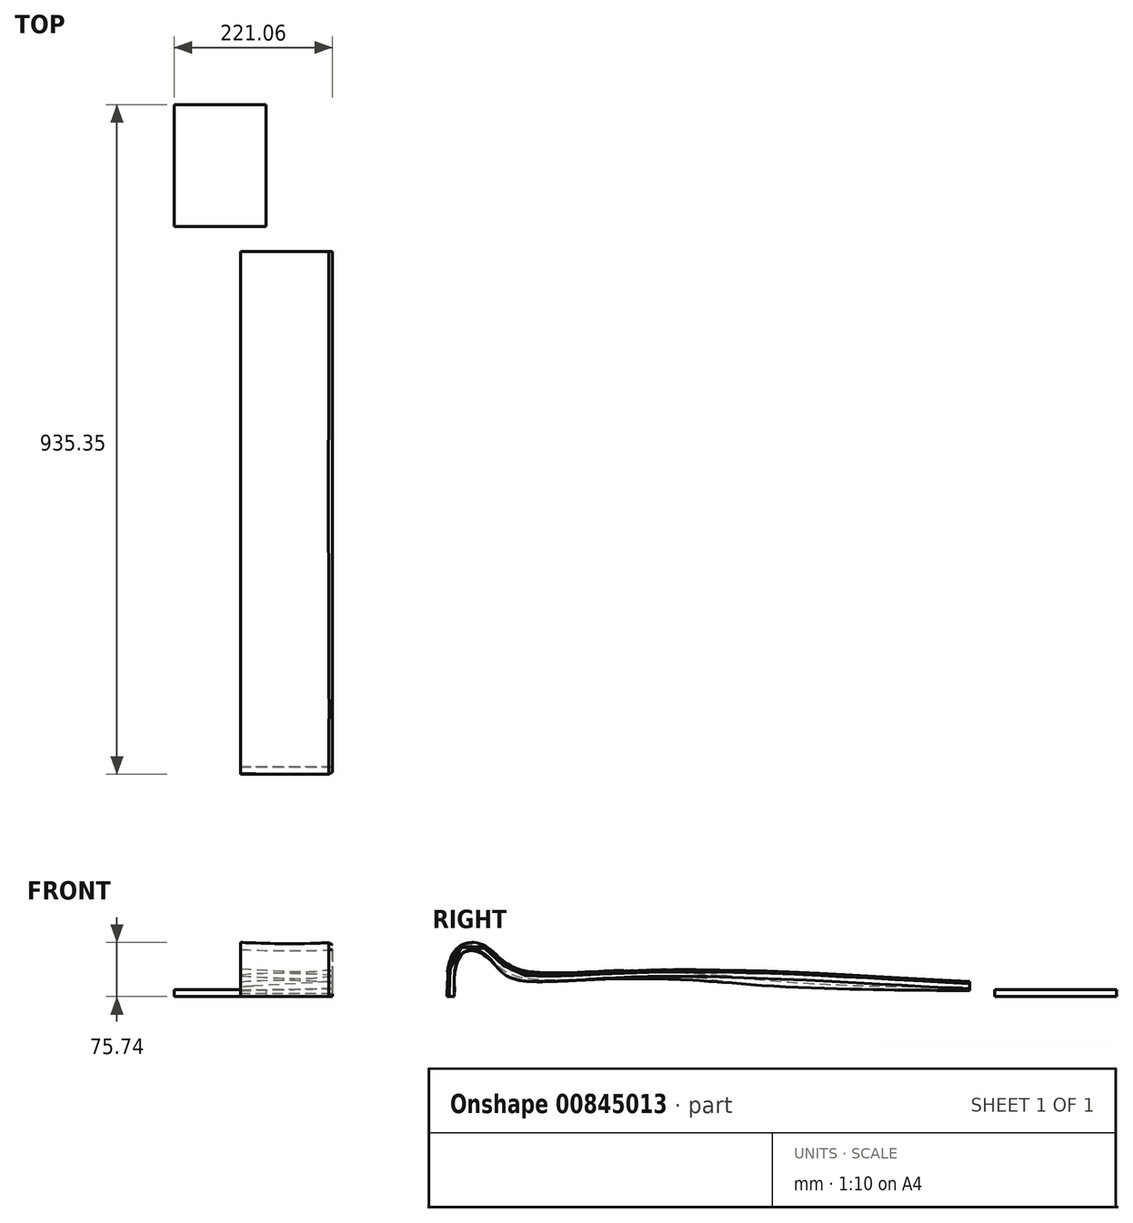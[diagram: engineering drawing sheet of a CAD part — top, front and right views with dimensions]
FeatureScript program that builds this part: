
annotation { "Feature Type Name" : "Feature", "Feature Type Description" : "" }
export const myFeature = defineFeature(function(context is Context, id is Id, definition is map)
    precondition{}
    {
        {
            var Q0;
            Q0=qCreatedBy(makeId("Right.planeOp"),FACE);
            var sketch = newSketch(context, id + "F0", { "sketchPlane" : qUnion([Q0])});
            skLineSegment(sketch, "E0", {"start": v(0, 4.3) * mm, "end": v(0, 0) * mm});
            skLineSegment(sketch, "E1", {"start": v(0, 0) * mm, "end": v(10, 0) * mm});
            skLineSegment(sketch, "E2", {"start": v(10, 0) * mm, "end": v(10, 4.3) * mm});
            skFitSpline(sketch, "E3", {"points": [v(10, 4.3) * mm, v(10, 9.47) * mm, v(10.81, 35.91) * mm, v(20.4, 60) * mm, v(37.7, 65.58) * mm, v(59.21, 54.06) * mm, v(82, 29.92) * mm, v(145.43, 21.16) * mm, v(328.73, 28.44) * mm, v(730, 11.2) * mm], "startDerivative": vector(2.28, 304.75) * mm, "endDerivative": vector(317.82, 1.74) * mm});
            skFitSpline(sketch, "E4", {"points": [v(0, 4.3) * mm, v(0, 9.47) * mm, v(0.81, 35.91) * mm, v(13.55, 67.28) * mm, v(37.7, 75.58) * mm, v(66.24, 61.18) * mm, v(87.9, 37.99) * mm, v(145.43, 31.16) * mm, v(328.73, 38.44) * mm, v(730, 21.2) * mm], "startDerivative": vector(0, 134.34) * mm, "endDerivative": vector(1575.84, -88.39) * mm});
            skLineSegment(sketch, "E5", {"start": v(730, 11.2) * mm, "end": v(730, 21.2) * mm});
            skSolve(sketch);
        }
        {
            var Q0;
            Q0=qCreatedBy(makeId("Right.planeOp"),FACE);
            cPlane(context, id + "F1", {"entities" : qUnion([Q0]), "cplaneType" : CPlaneType.OFFSET, "offset" : 128.5 * mm, "oppositeDirection" : true, "width" : 152.4 * mm, "height" : 152.4 * mm});
        }
        {
            var Q0;
            Q0=qCreatedBy(id+"F1.planeOp",FACE);
            var sketch = newSketch(context, id + "F2", { "sketchPlane" : qUnion([Q0])});
            skLineSegment(sketch, "E6", {"start": v(0, 4.3) * mm, "end": v(0, 0) * mm});
            skLineSegment(sketch, "E7", {"start": v(0, 0) * mm, "end": v(10, 0) * mm});
            skLineSegment(sketch, "E8", {"start": v(10, 0) * mm, "end": v(10, 4.3) * mm});
            skFitSpline(sketch, "E9", {"points": [v(10, 4.3) * mm, v(10.47, 9.4) * mm, v(10.81, 35.91) * mm, v(20.4, 60) * mm, v(37.7, 65.58) * mm, v(59.21, 54.06) * mm, v(82, 29.92) * mm, v(145.43, 21.16) * mm, v(328.73, 28.44) * mm, v(402.6, 19.18) * mm, v(589.23, 10) * mm, v(694, 8.62) * mm, v(730, 8.52) * mm], "startDerivative": vector(51.41, 302.7) * mm, "endDerivative": vector(431.3, 10.14) * mm});
            skFitSpline(sketch, "E10", {"points": [v(0, 4.3) * mm, v(0.47, 9.4) * mm, v(0.81, 35.91) * mm, v(13.55, 67.28) * mm, v(37.7, 75.58) * mm, v(66.24, 61.18) * mm, v(87.9, 37.99) * mm, v(145.43, 31.16) * mm, v(328.73, 38.44) * mm, v(402.6, 27.68) * mm, v(589.23, 15) * mm, v(694, 13.62) * mm, v(730, 13.52) * mm], "startDerivative": vector(0, 134.34) * mm, "endDerivative": vector(521.26, 14.92) * mm});
            skLineSegment(sketch, "E11", {"start": v(730, 8.52) * mm, "end": v(730, 13.52) * mm});
            skSolve(sketch);
        }
        {
            var Q0;
            Q0=makeQuery(id+"F0.imprint","IMPRINT",FACE,{"disambiguationData":[TD([[makeQuery(id+"F0.imprint","IMPRINT",EDGE,{"derivedFrom":sQuery(id+"F0.wireOp",EDGE,"E0")}),1.0]])]});
            var Q1;
            Q1=makeQuery(id+"F2.imprint","IMPRINT",FACE,{"disambiguationData":[TD([[makeQuery(id+"F2.imprint","IMPRINT",EDGE,{"derivedFrom":sQuery(id+"F2.wireOp",EDGE,"E6")}),1.0]])]});
            loft(context, id + "F3", {"sheetProfilesArray" : [{ "sheetProfileEntities" : qUnion([Q0]) }, { "sheetProfileEntities" : qUnion([Q1]) }]});
        }
        {
            var Q0;
            Q0=qCreatedBy(makeId("Top.planeOp"),FACE);
            var sketch = newSketch(context, id + "F4", { "sketchPlane" : qUnion([Q0])});
            skLineSegment(sketch, "E12.bottom", {"start": v(-221.06, 935.2) * mm, "end": v(-92.56, 935.2) * mm});
            skLineSegment(sketch, "E12.top", {"start": v(-221.06, 765.2) * mm, "end": v(-92.56, 765.2) * mm});
            skLineSegment(sketch, "E12.left", {"start": v(-221.06, 935.2) * mm, "end": v(-221.06, 765.2) * mm});
            skLineSegment(sketch, "E12.right", {"start": v(-92.56, 935.2) * mm, "end": v(-92.56, 765.2) * mm});
            skLineSegment(sketch, "E13", {"start": v(-221.06, 835.2) * mm, "end": v(-92.56, 835.2) * mm, "construction": true});
            skSolve(sketch);
        }
        {
            var Q0;
            Q0=makeQuery(id+"F4.imprint","IMPRINT",FACE,{"disambiguationData":[TD([[makeQuery(id+"F4.imprint","IMPRINT",EDGE,{"derivedFrom":sQuery(id+"F4.wireOp",EDGE,"E12.bottom")}),-1.0]])]});
            extrude(context, id + "F5", {"entities" : qUnion([Q0]), "depth" : 10 * mm, "offsetDistance" : 25.4 * mm});
        }
        {
            var Q0;
            Q0=makeQuery(id+"F3.opLoft","MID_CAP_EDGE",EDGE,{"disambiguationData":[OSD([sQuery(id+"F0.wireOp",EDGE,"E0"),sQuery(id+"F0.wireOp",EDGE,"E4"),sQuery(id+"F0.wireOp",EDGE,"E5")])],"capPos":0.0});
            chamfer(context, id + "F6", {"entities" : qUnion([Q0]), "chamferType" : ChamferType.OFFSET_ANGLE, "width" : 5.08 * mm, "oppositeDirection" : false, "angle" : 30 * degree, "tangentPropagation" : true});
        }
    });
